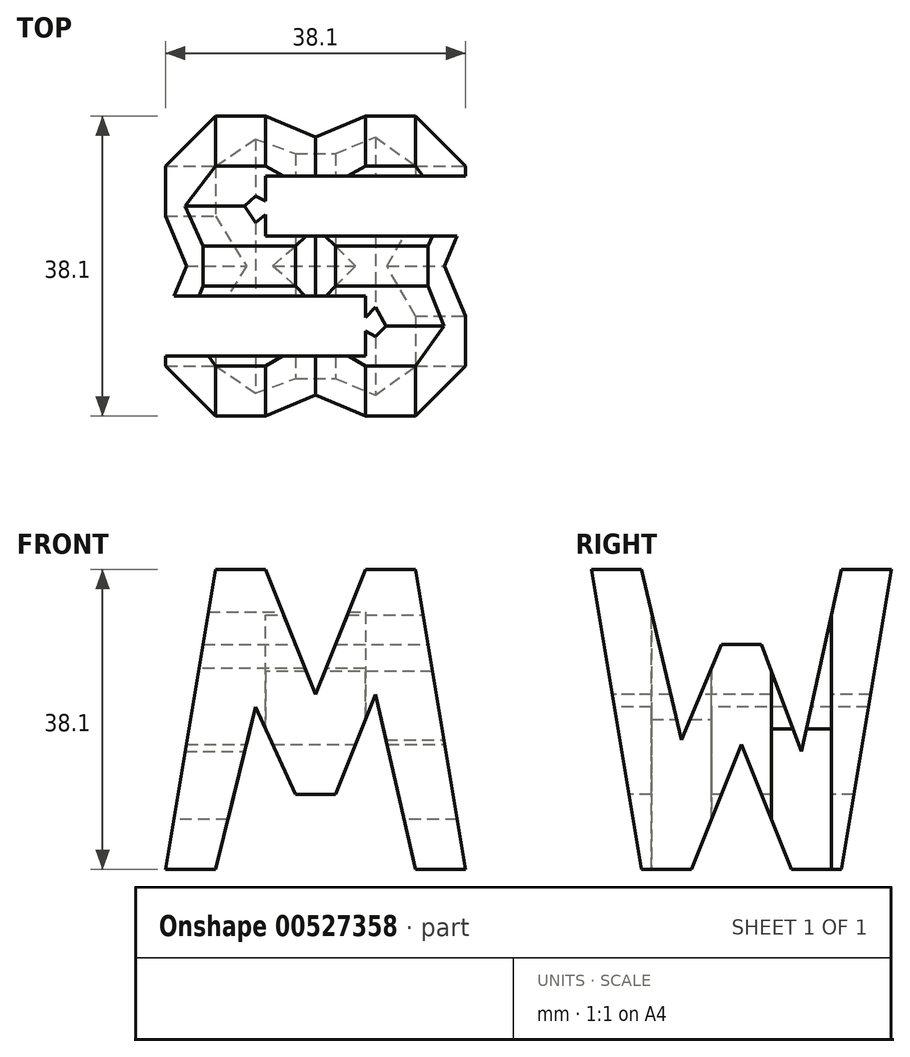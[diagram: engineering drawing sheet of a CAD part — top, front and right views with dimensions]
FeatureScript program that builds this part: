
annotation { "Feature Type Name" : "Feature", "Feature Type Description" : "" }
export const myFeature = defineFeature(function(context is Context, id is Id, definition is map)
    precondition{}
    {
        {
            var Q0;
            Q0=qCreatedBy(makeId("Front.planeOp"),FACE);
            var sketch = newSketch(context, id + "F0", { "sketchPlane" : qUnion([Q0])});
            skLineSegment(sketch, "E0", {"start": v(0, 0) * mm, "end": v(38.1, 0) * mm});
            skLineSegment(sketch, "E1", {"start": v(38.1, 0) * mm, "end": v(38.1, 38.1) * mm});
            skLineSegment(sketch, "E2", {"start": v(38.1, 38.1) * mm, "end": v(0, 38.1) * mm});
            skLineSegment(sketch, "E3", {"start": v(0, 38.1) * mm, "end": v(0, 0) * mm});
            skSolve(sketch);
        }
        {
            var Q0;
            Q0=qSketchRegion(id+"F0",true);
            extrude(context, id + "F1", {"entities" : qUnion([Q0]), "depth" : 38.1 * mm});
        }
        {
            var Q0;
            Q0=qCreatedBy(makeId("Front.planeOp"),FACE);
            cPlane(context, id + "F2", {"entities" : qUnion([Q0]), "cplaneType" : CPlaneType.OFFSET, "offset" : 38.1 * mm, "width" : 152.4 * mm, "height" : 152.4 * mm});
        }
        {
            var Q0;
            Q0=qCreatedBy(makeId("Right.planeOp"),FACE);
            cPlane(context, id + "F3", {"entities" : qUnion([Q0]), "cplaneType" : CPlaneType.OFFSET, "offset" : 38.1 * mm, "width" : 152.4 * mm, "height" : 152.4 * mm});
        }
        {
            var Q0;
            Q0=qCreatedBy(makeId("Top.planeOp"),FACE);
            cPlane(context, id + "F4", {"entities" : qUnion([Q0]), "cplaneType" : CPlaneType.OFFSET, "offset" : 38.1 * mm, "width" : 152.4 * mm, "height" : 152.4 * mm});
        }
        {
            var Q0;
            Q0=qCreatedBy(id+"F3.planeOp",FACE);
            var sketch = newSketch(context, id + "F5", { "sketchPlane" : qUnion([Q0])});
            skLineSegment(sketch, "E4", {"start": v(0, 0) * mm, "end": v(0, 38.1) * mm});
            skLineSegment(sketch, "E5", {"start": v(0, 38.1) * mm, "end": v(-38.1, 38.1) * mm});
            skLineSegment(sketch, "E6", {"start": v(-38.1, 38.1) * mm, "end": v(-38.1, 0) * mm});
            skLineSegment(sketch, "E7", {"start": v(-38.1, 0) * mm, "end": v(0, 0) * mm});
            skLineSegment(sketch, "E8", {"start": v(-38.1, 38.1) * mm, "end": v(-31.75, 0) * mm});
            skLineSegment(sketch, "E9", {"start": v(-25.4, 0) * mm, "end": v(-19.05, 15.88) * mm});
            skLineSegment(sketch, "E10", {"start": v(-19.05, 15.88) * mm, "end": v(-12.7, 0) * mm});
            skLineSegment(sketch, "E11", {"start": v(0, 38.1) * mm, "end": v(-6.35, 0) * mm});
            skLineSegment(sketch, "E12", {"start": v(-31.75, 38.1) * mm, "end": v(-26.67, 16.45) * mm});
            skLineSegment(sketch, "E13", {"start": v(-26.67, 16.45) * mm, "end": v(-21.59, 28.58) * mm});
            skLineSegment(sketch, "E14", {"start": v(-21.59, 28.58) * mm, "end": v(-16.5, 28.58) * mm});
            skLineSegment(sketch, "E15", {"start": v(-16.5, 28.58) * mm, "end": v(-11.43, 14.97) * mm});
            skLineSegment(sketch, "E16", {"start": v(-11.43, 14.97) * mm, "end": v(-6.35, 38.1) * mm});
            skSolve(sketch);
        }
        {
            var Q0;
            {var subQ0=sQuery(id+"F5.wireOp",EDGE,"E6");Q0=makeQuery(id+"F5.imprint","IMPRINT",FACE,{"disambiguationData":[TD([[makeQuery(id+"F5.imprint","IMPRINT",EDGE,{"derivedFrom":subQ0}),1.0]])]});}
            var Q1;
            {var subQ0=sQuery(id+"F5.wireOp",EDGE,"E12");Q1=makeQuery(id+"F5.imprint","IMPRINT",FACE,{"disambiguationData":[TD([[makeQuery(id+"F5.imprint","IMPRINT",EDGE,{"derivedFrom":subQ0}),1.0]])]});}
            var Q2;
            {var subQ0=sQuery(id+"F5.wireOp",EDGE,"E9");Q2=makeQuery(id+"F5.imprint","IMPRINT",FACE,{"disambiguationData":[TD([[makeQuery(id+"F5.imprint","IMPRINT",EDGE,{"derivedFrom":subQ0}),-1.0]])]});}
            var Q3;
            {var subQ0=sQuery(id+"F5.wireOp",EDGE,"E4");Q3=makeQuery(id+"F5.imprint","IMPRINT",FACE,{"disambiguationData":[TD([[makeQuery(id+"F5.imprint","IMPRINT",EDGE,{"derivedFrom":subQ0}),1.0]])]});}
            extrude(context, id + "F6", {"entities" : qUnion([Q0, Q1, Q2, Q3]), "operationType" : NewBodyOperationType.REMOVE, "oppositeDirection" : true, "depth" : 38.1 * mm});
        }
        {
            var Q0;
            Q0=qCreatedBy(id+"F2.planeOp",FACE);
            var sketch = newSketch(context, id + "F7", { "sketchPlane" : qUnion([Q0])});
            skLineSegment(sketch, "E17", {"start": v(0, 0) * mm, "end": v(38.1, 0) * mm});
            skLineSegment(sketch, "E18", {"start": v(38.1, 0) * mm, "end": v(38.1, 38.1) * mm});
            skLineSegment(sketch, "E19", {"start": v(38.1, 38.1) * mm, "end": v(0, 38.1) * mm});
            skLineSegment(sketch, "E20", {"start": v(0, 38.1) * mm, "end": v(0, 0) * mm});
            skLineSegment(sketch, "E21", {"start": v(6.35, 38.1) * mm, "end": v(0, 0) * mm});
            skLineSegment(sketch, "E22", {"start": v(12.7, 38.1) * mm, "end": v(19.05, 22.23) * mm});
            skPoint(sketch, "E22.endSnap0", {"position": v(19.05, 38.1) * mm});
            skLineSegment(sketch, "E23", {"start": v(19.05, 22.23) * mm, "end": v(25.4, 38.1) * mm});
            skLineSegment(sketch, "E24", {"start": v(31.75, 38.1) * mm, "end": v(38.1, 0) * mm});
            skLineSegment(sketch, "E25", {"start": v(6.35, 0) * mm, "end": v(11.43, 20.62) * mm});
            skLineSegment(sketch, "E26", {"start": v(11.43, 20.62) * mm, "end": v(16.51, 9.53) * mm});
            skLineSegment(sketch, "E27", {"start": v(16.51, 9.53) * mm, "end": v(21.6, 9.53) * mm});
            skLineSegment(sketch, "E28", {"start": v(21.6, 9.53) * mm, "end": v(26.67, 22.23) * mm});
            skLineSegment(sketch, "E29", {"start": v(26.67, 22.23) * mm, "end": v(31.75, 0) * mm});
            skSolve(sketch);
        }
        {
            var Q0;
            {var subQ0=sQuery(id+"F7.wireOp",EDGE,"E20");Q0=makeQuery(id+"F7.imprint","IMPRINT",FACE,{"disambiguationData":[TD([[makeQuery(id+"F7.imprint","IMPRINT",EDGE,{"derivedFrom":subQ0}),1.0]])]});}
            var Q1;
            {var subQ0=sQuery(id+"F7.wireOp",EDGE,"E22");Q1=makeQuery(id+"F7.imprint","IMPRINT",FACE,{"disambiguationData":[TD([[makeQuery(id+"F7.imprint","IMPRINT",EDGE,{"derivedFrom":subQ0}),1.0]])]});}
            var Q2;
            {var subQ0=sQuery(id+"F7.wireOp",EDGE,"E25");Q2=makeQuery(id+"F7.imprint","IMPRINT",FACE,{"disambiguationData":[TD([[makeQuery(id+"F7.imprint","IMPRINT",EDGE,{"derivedFrom":subQ0}),-1.0]])]});}
            var Q3;
            {var subQ0=sQuery(id+"F7.wireOp",EDGE,"E18");Q3=makeQuery(id+"F7.imprint","IMPRINT",FACE,{"disambiguationData":[TD([[makeQuery(id+"F7.imprint","IMPRINT",EDGE,{"derivedFrom":subQ0}),1.0]])]});}
            extrude(context, id + "F8", {"entities" : qUnion([Q0, Q1, Q2, Q3]), "operationType" : NewBodyOperationType.REMOVE, "oppositeDirection" : true, "depth" : 38.1 * mm});
        }
        {
            var Q0;
            Q0=qCreatedBy(id+"F4.planeOp",FACE);
            var sketch = newSketch(context, id + "F9", { "sketchPlane" : qUnion([Q0])});
            skLineSegment(sketch, "E30", {"start": v(0, 0) * mm, "end": v(38.1, 0) * mm});
            skLineSegment(sketch, "E31", {"start": v(38.1, 0) * mm, "end": v(38.1, -38.1) * mm});
            skLineSegment(sketch, "E32", {"start": v(38.1, -38.1) * mm, "end": v(0, -38.1) * mm});
            skLineSegment(sketch, "E33", {"start": v(0, -38.1) * mm, "end": v(0, 0) * mm});
            skLineSegment(sketch, "E34", {"start": v(38.1, -7.62) * mm, "end": v(12.7, -7.62) * mm});
            skLineSegment(sketch, "E35", {"start": v(12.7, -7.62) * mm, "end": v(12.7, -15.24) * mm});
            skLineSegment(sketch, "E36", {"start": v(12.7, -15.24) * mm, "end": v(38.1, -15.24) * mm});
            skLineSegment(sketch, "E37", {"start": v(0, -22.86) * mm, "end": v(25.4, -22.86) * mm});
            skLineSegment(sketch, "E38", {"start": v(25.4, -22.86) * mm, "end": v(25.4, -30.48) * mm});
            skLineSegment(sketch, "E39", {"start": v(25.4, -30.48) * mm, "end": v(0, -30.48) * mm});
            skSolve(sketch);
        }
        {
            var Q0;
            {var subQ0=sQuery(id+"F9.wireOp",EDGE,"E34");Q0=makeQuery(id+"F9.imprint","IMPRINT",FACE,{"disambiguationData":[TD([[makeQuery(id+"F9.imprint","IMPRINT",EDGE,{"derivedFrom":subQ0}),1.0]])]});}
            var Q1;
            {var subQ0=sQuery(id+"F9.wireOp",EDGE,"E37");Q1=makeQuery(id+"F9.imprint","IMPRINT",FACE,{"disambiguationData":[TD([[makeQuery(id+"F9.imprint","IMPRINT",EDGE,{"derivedFrom":subQ0}),-1.0]])]});}
            extrude(context, id + "F10", {"entities" : qUnion([Q0, Q1]), "operationType" : NewBodyOperationType.REMOVE, "oppositeDirection" : true, "depth" : 38.1 * mm});
        }
    });
